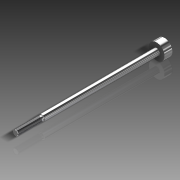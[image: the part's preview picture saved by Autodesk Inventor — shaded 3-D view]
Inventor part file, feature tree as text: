
AUTODESK INVENTOR PART (.ipt)
format: ipt  version: 2011 (Build 150239000, 239)  size: 88,064 bytes
history: native  units: in
note: dims shown in document units (in); Inventor stores cm internally (conversion verified against a paired STEP export)
features: thread x2, imported_body x1
ambient origin geometry x8: Origin, YZ Plane, XZ Plane, XY Plane, X Axis, Y Axis, Z Axis, Center Point
feature tree (3):
  thread  "Threads"  [1 undecoded]
  imported_body  "Base1"
  thread  "Thread1"  [1 undecoded]
note: 2 required parameter values undecoded (feature->parameter linkage not recoverable at this tier; creation-order binding heuristic only, values carry confidence <= 0.55)
